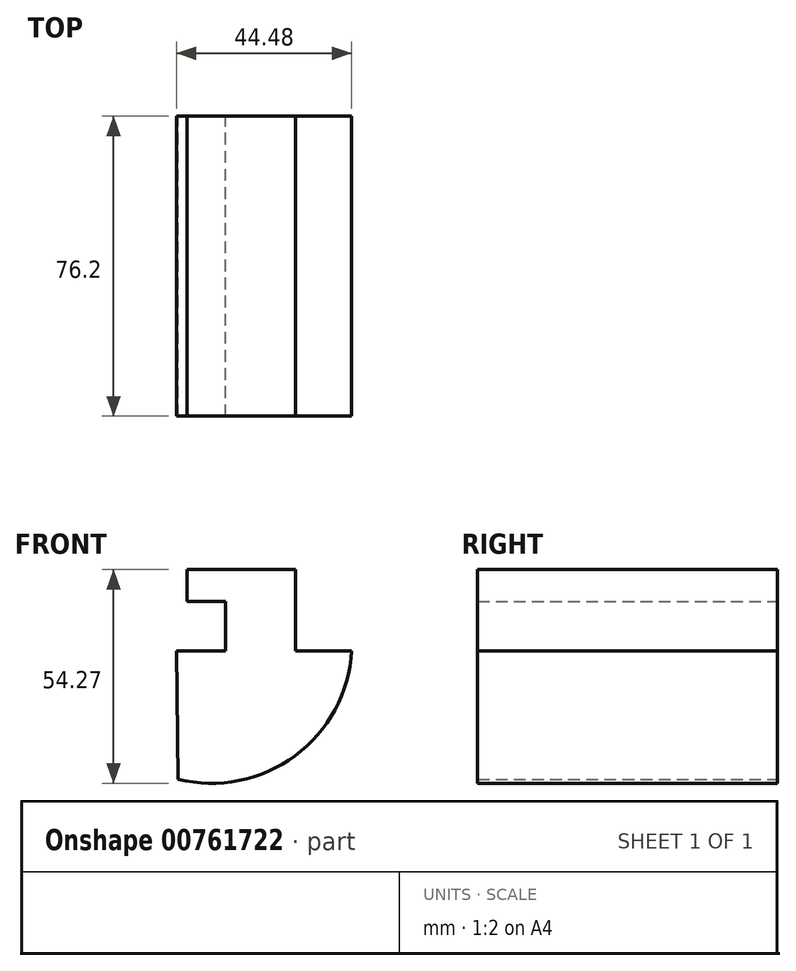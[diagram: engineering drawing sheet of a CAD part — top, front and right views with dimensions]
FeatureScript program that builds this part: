
annotation { "Feature Type Name" : "Feature", "Feature Type Description" : "" }
export const myFeature = defineFeature(function(context is Context, id is Id, definition is map)
    precondition{}
    {
        {
            var Q0;
            Q0=qCreatedBy(makeId("Front.planeOp"),FACE);
            var sketch = newSketch(context, id + "F0", { "sketchPlane" : qUnion([Q0])});
            skArc(sketch, "E0", {"start": v(-75.51, -72.2) * mm, "mid": v(-45.78, -66.26) * mm, "end": v(-31.34, -39.6) * mm});
            skLineSegment(sketch, "E1", {"start": v(-31.34, -39.6) * mm, "end": v(-75.82, -39.6) * mm});
            skLineSegment(sketch, "E2", {"start": v(-75.82, -39.6) * mm, "end": v(-75.51, -72.2) * mm});
            skLineSegment(sketch, "E3", {"start": v(-63.35, -18.96) * mm, "end": v(-73.23, -18.96) * mm});
            skLineSegment(sketch, "E4", {"start": v(-73.23, -18.96) * mm, "end": v(-73.23, -27.08) * mm});
            skLineSegment(sketch, "E5", {"start": v(-73.23, -27.08) * mm, "end": v(-63.35, -27.08) * mm});
            skLineSegment(sketch, "E6", {"start": v(-45.6, -39.6) * mm, "end": v(-45.6, -18.96) * mm});
            skLineSegment(sketch, "E7", {"start": v(-63.35, -18.96) * mm, "end": v(-45.6, -18.96) * mm});
            skLineSegment(sketch, "E8", {"start": v(-63.35, -27.08) * mm, "end": v(-63.35, -39.6) * mm});
            skSolve(sketch);
        }
        {
            var Q0;
            Q0 = qSketchRegion(id + "F0", true);
            extrude(context, id + "F1", {"entities" : qUnion([Q0]), "depth" : 76.2 * mm, "offsetDistance" : 25.4 * mm});
        }
    });
